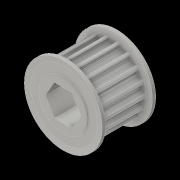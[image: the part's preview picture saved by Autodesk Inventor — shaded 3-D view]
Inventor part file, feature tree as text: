
AUTODESK INVENTOR PART (.ipt)
format: ipt  version: 2016 (Build 200138000, 138)  size: 645,632 bytes
history: native  units: in
note: dims shown in document units (in); Inventor stores cm internally (conversion verified against a paired STEP export)
features: mirror x1
ambient origin geometry x8: Origin, YZ Plane, XZ Plane, XY Plane, X Axis, Y Axis, Z Axis, Center Point
bodies: Solid1 (feature_tree)
feature tree (1):
  mirror  "Mirror1"
